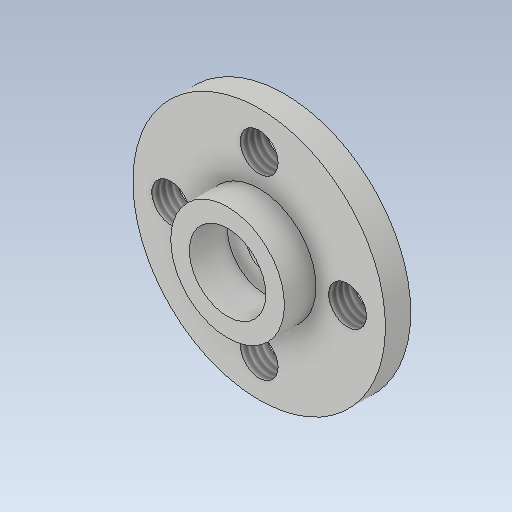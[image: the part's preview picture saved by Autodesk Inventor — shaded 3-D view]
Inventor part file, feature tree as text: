
AUTODESK INVENTOR PART (.ipt)
format: ipt  version: 2020.1 (Build 241239000, 239)  size: 160,768 bytes
history: native  units: mm
features: extrude x6, sketch x6, thread x4
ambient origin geometry x8: Origin, YZ Plane, XZ Plane, XY Plane, X Axis, Y Axis, Z Axis, Center Point
bodies: Solid1 (feature_tree)
feature tree (16):
  extrude  "Extrusion1"  Depth=2.0mm TaperAngle=0.0deg
  extrude  "Extrusion2"  Depth=2.5mm TaperAngle=0.0deg
  extrude  "Extrusion3"  Depth=2.5mm TaperAngle=0.0deg
  extrude  "Extrusion4"  Depth=2.5mm TaperAngle=0.0deg
  extrude  "Extrusion5"  Depth=3.0mm
  thread  "Thread1"  [1 undecoded]
  thread  "Thread2"  [1 undecoded]
  thread  "Thread3"  [1 undecoded]
  thread  "Thread4"  [1 undecoded]
  extrude  "Extrusion6"  Depth=10.0mm TaperAngle=0.0deg
  sketch  "Sketch1"  dims[d0=20.0mm d1=2.0mm d2=0.0mm]
  sketch  "Sketch2"  dims[d3=9.0mm d4=2.5mm d5=0.0mm]
  sketch  "Sketch3"  dims[d6=3.0mm d7=2.5mm d8=0.0mm]
  sketch  "Sketch4"  dims[d9=6.05mm d10=2.5mm d11=0.0mm]
  sketch  "Sketch5"  dims[d12=7.0mm d13=3.0mm d14=40.0mm d16=360.0deg d18=2.5mm d19=0.0mm d20=10.0mm d21=0.0mm d22=10.0mm d23=0.0mm]
  sketch  "Sketch6"  dims[d24=10.0mm d25=0.0mm d26=10.0mm d27=0.0mm d28=0.5mm d29=0.0mm]
note: 4 required parameter values undecoded (feature->parameter linkage not recoverable at this tier; creation-order binding heuristic only, values carry confidence <= 0.55)
